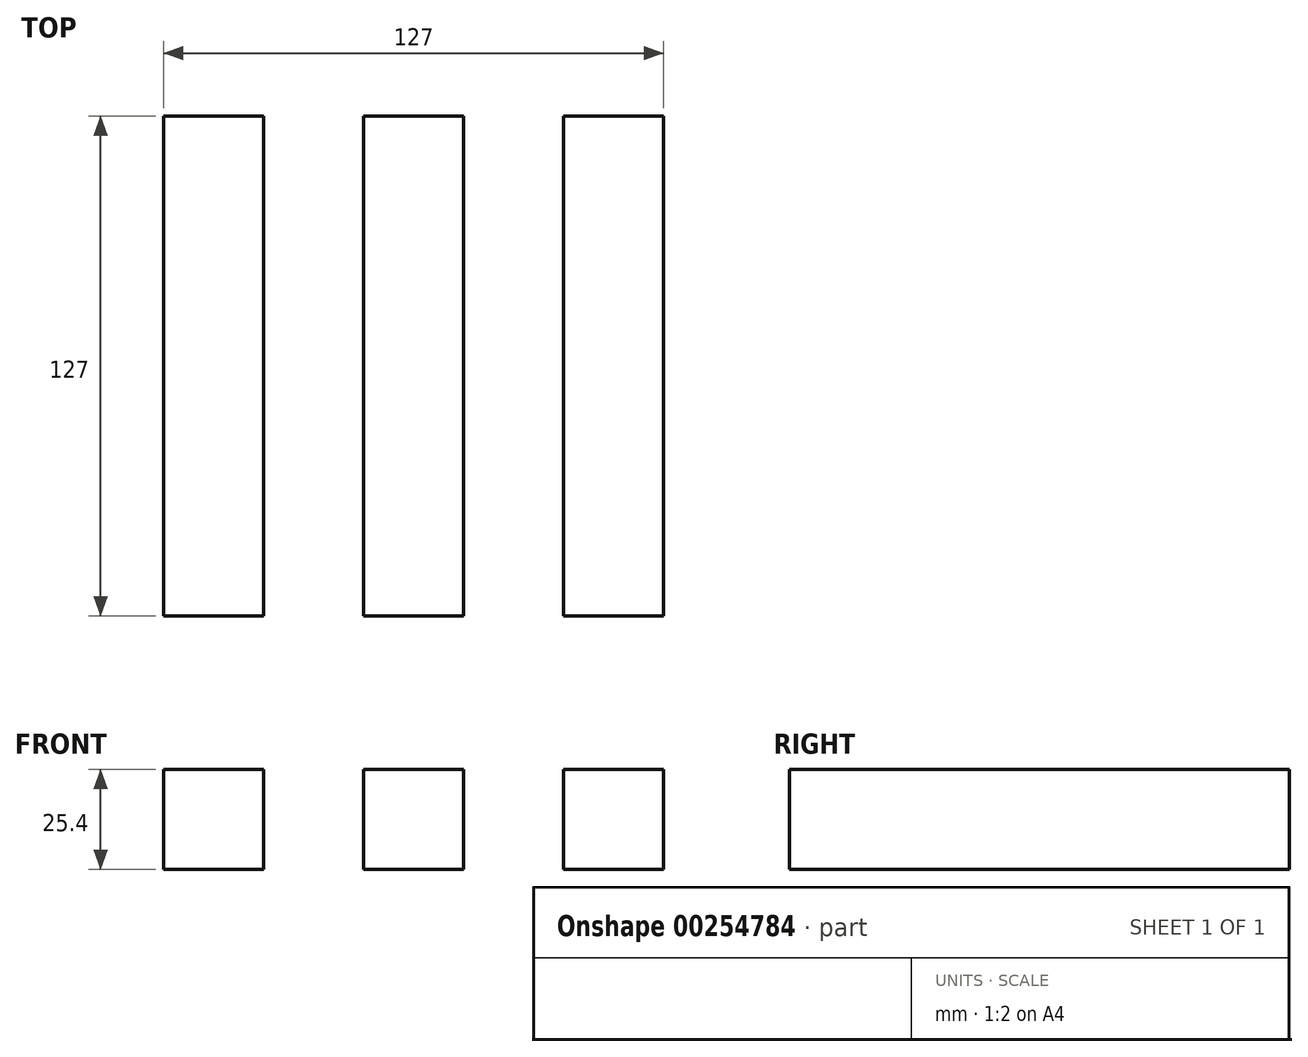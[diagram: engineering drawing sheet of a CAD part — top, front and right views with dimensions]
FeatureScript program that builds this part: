
annotation { "Feature Type Name" : "Feature", "Feature Type Description" : "" }
export const myFeature = defineFeature(function(context is Context, id is Id, definition is map)
    precondition{}
    {
        {
            var Q0;
            Q0=qCreatedBy(makeId("Front.planeOp"),FACE);
            var sketch = newSketch(context, id + "F0", { "sketchPlane" : qUnion([Q0])});
            skLineSegment(sketch, "E0.bottom", {"start": v(12.7, -12.7) * mm, "end": v(-12.7, -12.7) * mm});
            skLineSegment(sketch, "E0.top", {"start": v(12.7, 12.7) * mm, "end": v(-12.7, 12.7) * mm});
            skLineSegment(sketch, "E0.left", {"start": v(12.7, -12.7) * mm, "end": v(12.7, 12.7) * mm});
            skLineSegment(sketch, "E0.right", {"start": v(-12.7, -12.7) * mm, "end": v(-12.7, 12.7) * mm});
            skPoint(sketch, "E0.middle", {"position": v(0, 0) * mm});
            skLineSegment(sketch, "E1.bottom", {"start": v(63.5, -12.7) * mm, "end": v(38.1, -12.7) * mm});
            skLineSegment(sketch, "E1.top", {"start": v(63.5, 12.7) * mm, "end": v(38.1, 12.7) * mm});
            skLineSegment(sketch, "E1.left", {"start": v(63.5, -12.7) * mm, "end": v(63.5, 12.7) * mm});
            skLineSegment(sketch, "E1.right", {"start": v(38.1, -12.7) * mm, "end": v(38.1, 12.7) * mm});
            skPoint(sketch, "E1.middle", {"position": v(50.8, 0) * mm});
            skLineSegment(sketch, "E2.bottom", {"start": v(-38.1, -12.7) * mm, "end": v(-63.5, -12.7) * mm});
            skLineSegment(sketch, "E2.top", {"start": v(-38.1, 12.7) * mm, "end": v(-63.5, 12.7) * mm});
            skLineSegment(sketch, "E2.left", {"start": v(-38.1, -12.7) * mm, "end": v(-38.1, 12.7) * mm});
            skLineSegment(sketch, "E2.right", {"start": v(-63.5, -12.7) * mm, "end": v(-63.5, 12.7) * mm});
            skPoint(sketch, "E2.middle", {"position": v(-50.8, 0) * mm});
            skSolve(sketch);
        }
        {
            var Q0;
            Q0=makeQuery(id+"F0.imprint","IMPRINT",FACE,{"disambiguationData":[TD([[makeQuery(id+"F0.imprint","IMPRINT",EDGE,{"derivedFrom":sQuery(id+"F0.wireOp",EDGE,"E1.bottom")}),-1.0]])]});
            var Q1;
            Q1=makeQuery(id+"F0.imprint","IMPRINT",FACE,{"disambiguationData":[TD([[makeQuery(id+"F0.imprint","IMPRINT",EDGE,{"derivedFrom":sQuery(id+"F0.wireOp",EDGE,"E0.bottom")}),-1.0]])]});
            var Q2;
            Q2=makeQuery(id+"F0.imprint","IMPRINT",FACE,{"disambiguationData":[TD([[makeQuery(id+"F0.imprint","IMPRINT",EDGE,{"derivedFrom":sQuery(id+"F0.wireOp",EDGE,"E2.bottom")}),-1.0]])]});
            var Q3;
            Q3 = qSketchRegion(id + "F0", true);
            extrude(context, id + "F1", {"entities" : qUnion([Q0, Q1, Q2, Q3]), "endBound" : BoundingType.SYMMETRIC, "depth" : 127 * mm});
        }
    });
